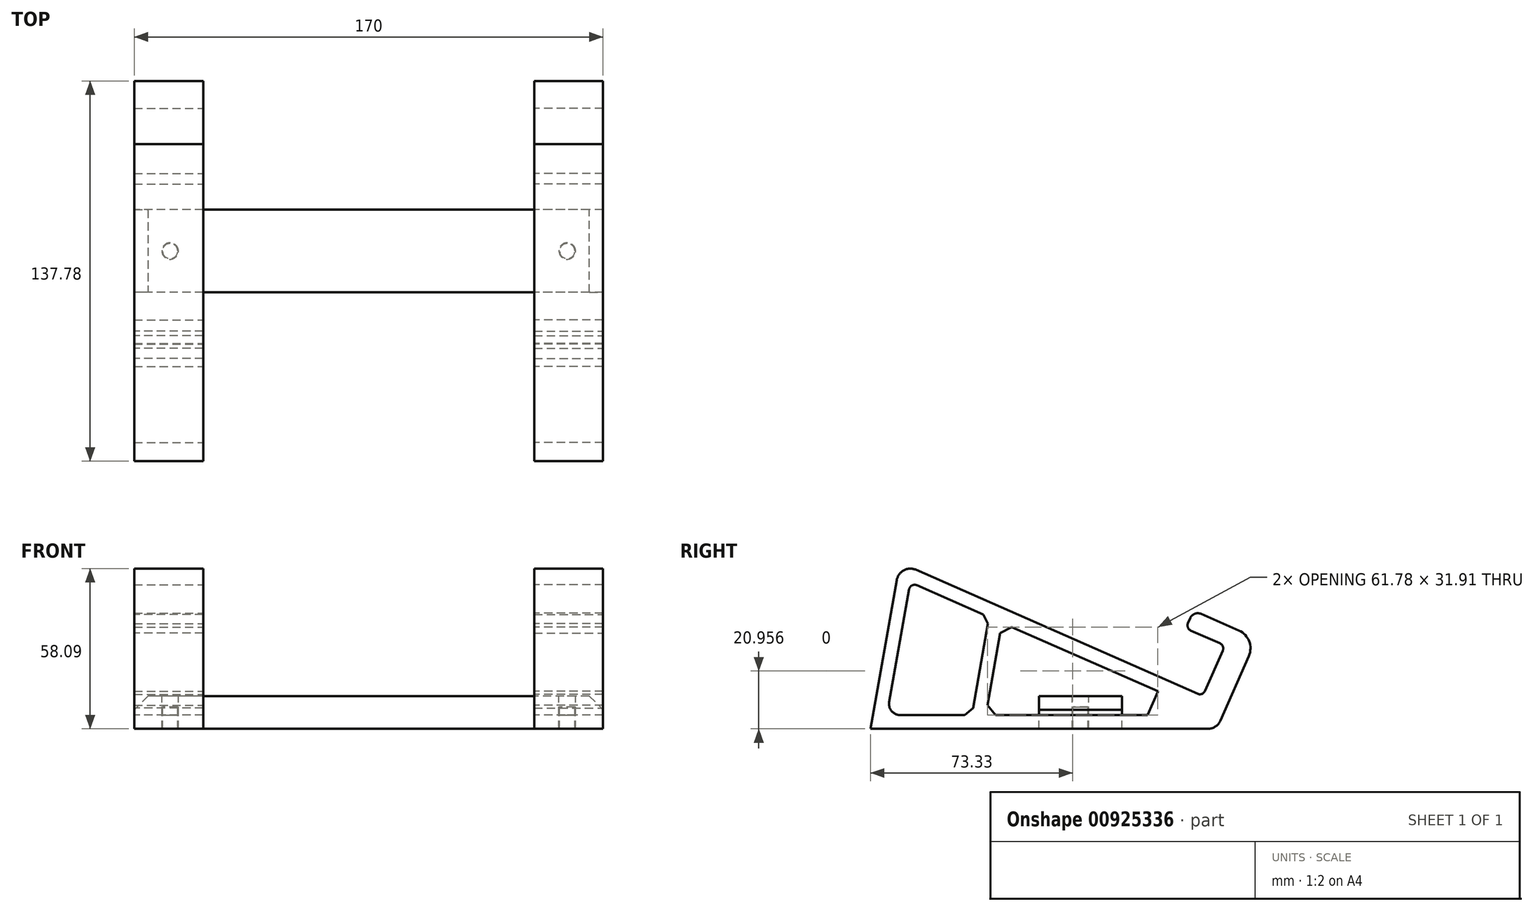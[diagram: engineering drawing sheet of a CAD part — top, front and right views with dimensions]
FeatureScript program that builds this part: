
annotation { "Feature Type Name" : "Feature", "Feature Type Description" : "" }
export const myFeature = defineFeature(function(context is Context, id is Id, definition is map)
    precondition{}
    {
        {
            var Q0;
            Q0=qCreatedBy(makeId("Right.planeOp"),FACE);
            cPlane(context, id + "F0", {"entities" : qUnion([Q0]), "cplaneType" : CPlaneType.OFFSET, "offset" : 60 * mm, "width" : 150 * mm, "height" : 150 * mm});
        }
        {
            var Q0;
            Q0=qCreatedBy(id+"F0.planeOp",FACE);
            var sketch = newSketch(context, id + "F1", { "sketchPlane" : qUnion([Q0])});
            skLineSegment(sketch, "E0", {"start": v(-1.83, 0.8) * mm, "end": v(-109.84, 48.33) * mm});
            skLineSegment(sketch, "E1", {"start": v(-109.84, 0) * mm, "end": v(0, 0) * mm, "construction": true});
            skLineSegment(sketch, "E2", {"start": v(0.8, 1.83) * mm, "end": v(7.25, 16.48) * mm});
            skLineSegment(sketch, "E3", {"start": v(6.22, 19.11) * mm, "end": v(-4.35, 23.76) * mm});
            skLineSegment(sketch, "E4", {"start": v(-5.37, 26.4) * mm, "end": v(-4.57, 28.23) * mm});
            skLineSegment(sketch, "E5", {"start": v(-0.61, 29.77) * mm, "end": v(13.12, 23.73) * mm});
            skLineSegment(sketch, "E6", {"start": v(16.7, 14.5) * mm, "end": v(0, -23.46) * mm});
            skLineSegment(sketch, "E7", {"start": v(5.09, -11.9) * mm, "end": v(-120.48, -11.9) * mm});
            skLineSegment(sketch, "E8", {"start": v(-109.84, 48.33) * mm, "end": v(-120.48, -11.9) * mm});
            skPoint(sketch, "E9.visualSharp", {"position": v(19.52, 20.9) * mm});
            skArc(sketch, "E9.filletArc", {"start": v(16.7, 14.5) * mm, "mid": v(16.82, 19.86) * mm, "end": v(13.12, 23.73) * mm});
            skPoint(sketch, "E10.visualSharp", {"position": v(-3.36, 30.98) * mm});
            skArc(sketch, "E10.filletArc", {"start": v(-0.61, 29.77) * mm, "mid": v(-2.9, 29.82) * mm, "end": v(-4.57, 28.23) * mm});
            skPoint(sketch, "E11.visualSharp", {"position": v(-6.18, 24.57) * mm});
            skArc(sketch, "E11.filletArc", {"start": v(-5.37, 26.4) * mm, "mid": v(-5.4, 24.87) * mm, "end": v(-4.35, 23.76) * mm});
            skPoint(sketch, "E12.visualSharp", {"position": v(8.05, 18.3) * mm});
            skArc(sketch, "E12.filletArc", {"start": v(7.25, 16.48) * mm, "mid": v(7.28, 18) * mm, "end": v(6.22, 19.11) * mm});
            skPoint(sketch, "E13.visualSharp", {"position": v(0, 0) * mm});
            skArc(sketch, "E13.filletArc", {"start": v(-1.83, 0.8) * mm, "mid": v(-0.3, 0.77) * mm, "end": v(0.8, 1.83) * mm});
            skSolve(sketch);
        }
        {
            var Q0;
            Q0 = qSketchRegion(id + "F1", true);
            extrude(context, id + "F2", {"entities" : qUnion([Q0]), "depth" : 25 * mm, "offsetDistance" : 25 * mm});
        }
        {
            var Q0;
            Q0=makeQuery(id+"F2.opExtrude","SWEPT_EDGE",EDGE,{"disambiguationData":[OSD([sQuery(id+"F1.wireOp",EDGE,"E0"),sQuery(id+"F1.wireOp",EDGE,"E8")])]});
            var Q1;
            Q1=makeQuery(id+"F2.opExtrude","SWEPT_EDGE",EDGE,{"disambiguationData":[OSD([sQuery(id+"F1.wireOp",EDGE,"E6"),sQuery(id+"F1.wireOp",EDGE,"E7")])]});
            fillet(context, id + "F3", {"entities" : qUnion([Q0, Q1]), "radius" : 5 * mm, "tangentPropagation" : true, "allowEdgeOverflow" : false});
        }
        {
            var Q0;
            Q0=qCreatedBy(makeId("Right.planeOp"),FACE);
            var sketch = newSketch(context, id + "F4", { "sketchPlane" : qUnion([Q0])});
            skLineSegment(sketch, "E14.0", {"start": v(-1.83, 0.8) * mm, "end": v(-104, 45.76) * mm, "construction": true});
            skLineSegment(sketch, "E15.0", {"start": v(1.83, -11.9) * mm, "end": v(-120.48, -11.9) * mm, "construction": true});
            skLineSegment(sketch, "E16.0", {"start": v(-16.26, 1.7) * mm, "end": v(-72.75, 26.55) * mm});
            skLineSegment(sketch, "E17.0", {"start": v(-20.04, -6.9) * mm, "end": v(-78.66, -6.9) * mm});
            skLineSegment(sketch, "E18", {"start": v(-16.26, 1.7) * mm, "end": v(-20.04, -6.9) * mm});
            skLineSegment(sketch, "E19.0", {"start": v(16.7, 14.5) * mm, "end": v(6.4, -8.91) * mm, "construction": true});
            skLineSegment(sketch, "E20.0", {"start": v(-106.46, 38.68) * mm, "end": v(-113.69, -2.2) * mm});
            skPoint(sketch, "E21.visualSharp", {"position": v(-106.02, 41.19) * mm});
            skArc(sketch, "E21.filletArc", {"start": v(-103.69, 40.16) * mm, "mid": v(-105.44, 40.1) * mm, "end": v(-106.46, 38.68) * mm});
            skPoint(sketch, "E22.visualSharp", {"position": v(-114.52, -6.9) * mm});
            skArc(sketch, "E22.filletArc", {"start": v(-113.69, -2.2) * mm, "mid": v(-112.81, -5.47) * mm, "end": v(-109.75, -6.9) * mm});
            skLineSegment(sketch, "E23", {"start": v(-77.46, 28.62) * mm, "end": v(-83.74, -6.9) * mm});
            skLineSegment(sketch, "E24.0", {"start": v(-72.75, 26.55) * mm, "end": v(-78.66, -6.9) * mm});
            skLineSegment(sketch, "E25.trimOffspring", {"start": v(-77.46, 28.62) * mm, "end": v(-103.69, 40.16) * mm});
            skLineSegment(sketch, "E26.trimOffspring", {"start": v(-83.74, -6.9) * mm, "end": v(-109.75, -6.9) * mm});
            skSolve(sketch);
        }
        {
            var Q0;
            Q0 = qSketchRegion(id + "F4", true);
            var Q1;
            Q1=makeQuery(id+"F2.opExtrude","CAP_FACE",FACE,{"disambiguationData":[OSD([sQuery(id+"F1.wireOp",EDGE,"E0"),sQuery(id+"F1.wireOp",EDGE,"E2"),sQuery(id+"F1.wireOp",EDGE,"E3"),sQuery(id+"F1.wireOp",EDGE,"E4"),sQuery(id+"F1.wireOp",EDGE,"E5"),sQuery(id+"F1.wireOp",EDGE,"E6"),sQuery(id+"F1.wireOp",EDGE,"E7"),sQuery(id+"F1.wireOp",EDGE,"E8"),sQuery(id+"F1.wireOp",EDGE,"E9.filletArc"),sQuery(id+"F1.wireOp",EDGE,"E10.filletArc"),sQuery(id+"F1.wireOp",EDGE,"E11.filletArc"),sQuery(id+"F1.wireOp",EDGE,"E12.filletArc"),sQuery(id+"F1.wireOp",EDGE,"E13.filletArc")])],"isStart":false});
            extrude(context, id + "F5", {"entities" : qUnion([Q0]), "operationType" : NewBodyOperationType.REMOVE, "endBound" : BoundingType.UP_TO_SURFACE, "depth" : 63 * mm, "endBoundEntityFace" : qUnion([Q1]), "offsetDistance" : 25 * mm});
        }
        {
            var Q0;
            Q0=makeQuery(id+"F5.boolean.opBoolean","COPY",EDGE,{"derivedFrom":makeQuery(id+"F5.opExtrude","SWEPT_EDGE",EDGE,{"disambiguationData":[OSD([sQuery(id+"F4.wireOp",EDGE,"E23"),sQuery(id+"F4.wireOp",EDGE,"E25.trimOffspring")])]})});
            var Q1;
            Q1=makeQuery(id+"F5.boolean.opBoolean","COPY",EDGE,{"derivedFrom":makeQuery(id+"F5.opExtrude","SWEPT_EDGE",EDGE,{"disambiguationData":[OSD([sQuery(id+"F4.wireOp",EDGE,"E16.0"),sQuery(id+"F4.wireOp",EDGE,"E24.0")])]})});
            var Q2;
            Q2=makeQuery(id+"F5.boolean.opBoolean","COPY",EDGE,{"derivedFrom":makeQuery(id+"F5.opExtrude","SWEPT_EDGE",EDGE,{"disambiguationData":[OSD([sQuery(id+"F4.wireOp",EDGE,"E23"),sQuery(id+"F4.wireOp",EDGE,"E26.trimOffspring")])]})});
            var Q3;
            Q3=makeQuery(id+"F5.boolean.opBoolean","COPY",EDGE,{"derivedFrom":makeQuery(id+"F5.opExtrude","SWEPT_EDGE",EDGE,{"disambiguationData":[OSD([sQuery(id+"F4.wireOp",EDGE,"E17.0"),sQuery(id+"F4.wireOp",EDGE,"E24.0")])]})});
            chamfer(context, id + "F6", {"entities" : qUnion([Q0, Q1, Q2, Q3]), "width" : 3 * mm, "tangentPropagation" : true});
        }
        {
            var Q0;
            Q0=makeQuery(id+"F2.opExtrude","SWEPT_BODY",BODY,{"disambiguationData":[OSD([sQuery(id+"F1.wireOp",EDGE,"E0"),sQuery(id+"F1.wireOp",EDGE,"E2"),sQuery(id+"F1.wireOp",EDGE,"E3"),sQuery(id+"F1.wireOp",EDGE,"E4"),sQuery(id+"F1.wireOp",EDGE,"E5"),sQuery(id+"F1.wireOp",EDGE,"E6"),sQuery(id+"F1.wireOp",EDGE,"E7"),sQuery(id+"F1.wireOp",EDGE,"E8"),sQuery(id+"F1.wireOp",EDGE,"E9.filletArc"),sQuery(id+"F1.wireOp",EDGE,"E10.filletArc"),sQuery(id+"F1.wireOp",EDGE,"E11.filletArc"),sQuery(id+"F1.wireOp",EDGE,"E12.filletArc"),sQuery(id+"F1.wireOp",EDGE,"E13.filletArc")])]});
            var Q1;
            Q1=qCreatedBy(makeId("Right.planeOp"),FACE);
            mirror(context, id + "F7", {"entities" : qUnion([Q0]), "mirrorPlane" : qUnion([Q1])});
        }
        {
            var Q0;
            Q0=qCreatedBy(makeId("Top.planeOp"),FACE);
            var sketch = newSketch(context, id + "F8", { "sketchPlane" : qUnion([Q0])});
            skLineSegment(sketch, "E27.bottom", {"start": v(85, -59.33) * mm, "end": v(-85, -59.33) * mm});
            skLineSegment(sketch, "E27.top", {"start": v(85, -29.33) * mm, "end": v(-85, -29.33) * mm});
            skLineSegment(sketch, "E27.left", {"start": v(85, -59.33) * mm, "end": v(85, -29.33) * mm});
            skLineSegment(sketch, "E27.right", {"start": v(-85, -59.33) * mm, "end": v(-85, -29.33) * mm});
            skPoint(sketch, "E27.middle", {"position": v(0, -44.33) * mm});
            skSolve(sketch);
        }
        {
            var Q0;
            Q0=makeQuery(id+"F8.imprint","IMPRINT",FACE,{"disambiguationData":[TD([[makeQuery(id+"F8.imprint","IMPRINT",EDGE,{"derivedFrom":sQuery(id+"F8.wireOp",EDGE,"E27.bottom")}),-1.0]])]});
            var Q1;
            Q1=makeQuery(id+"F2.opExtrude","SWEPT_FACE",FACE,{"disambiguationData":[OSD([sQuery(id+"F1.wireOp",EDGE,"E7")])]});
            extrude(context, id + "F9", {"entities" : qUnion([Q0]), "endBound" : BoundingType.UP_TO_SURFACE, "oppositeDirection" : true, "depth" : 25 * mm, "endBoundEntityFace" : qUnion([Q1]), "offsetDistance" : 25 * mm});
        }
        {
            var Q0;
            Q0=makeQuery(id+"F9.opExtrude","CAP_EDGE",EDGE,{"disambiguationData":[OSD([sQuery(id+"F8.wireOp",EDGE,"E27.left")])],"isStart":true});
            var Q1;
            Q1=makeQuery(id+"F9.opExtrude","CAP_EDGE",EDGE,{"disambiguationData":[OSD([sQuery(id+"F8.wireOp",EDGE,"E27.right")])],"isStart":true});
            chamfer(context, id + "F10", {"entities" : qUnion([Q0, Q1]), "width" : 5 * mm, "tangentPropagation" : true});
        }
        {
            var Q0;
            Q0=makeQuery(id+"F7.opPattern","COPY",BODY,{"derivedFrom":makeQuery(id+"F2.opExtrude","SWEPT_BODY",BODY,{"disambiguationData":[OSD([sQuery(id+"F1.wireOp",EDGE,"E0"),sQuery(id+"F1.wireOp",EDGE,"E2"),sQuery(id+"F1.wireOp",EDGE,"E3"),sQuery(id+"F1.wireOp",EDGE,"E4"),sQuery(id+"F1.wireOp",EDGE,"E5"),sQuery(id+"F1.wireOp",EDGE,"E6"),sQuery(id+"F1.wireOp",EDGE,"E7"),sQuery(id+"F1.wireOp",EDGE,"E8"),sQuery(id+"F1.wireOp",EDGE,"E9.filletArc"),sQuery(id+"F1.wireOp",EDGE,"E10.filletArc"),sQuery(id+"F1.wireOp",EDGE,"E11.filletArc"),sQuery(id+"F1.wireOp",EDGE,"E12.filletArc"),sQuery(id+"F1.wireOp",EDGE,"E13.filletArc")])]}),"instanceName":"1"});
            var Q1;
            Q1=makeQuery(id+"F2.opExtrude","SWEPT_BODY",BODY,{"disambiguationData":[OSD([sQuery(id+"F1.wireOp",EDGE,"E0"),sQuery(id+"F1.wireOp",EDGE,"E2"),sQuery(id+"F1.wireOp",EDGE,"E3"),sQuery(id+"F1.wireOp",EDGE,"E4"),sQuery(id+"F1.wireOp",EDGE,"E5"),sQuery(id+"F1.wireOp",EDGE,"E6"),sQuery(id+"F1.wireOp",EDGE,"E7"),sQuery(id+"F1.wireOp",EDGE,"E8"),sQuery(id+"F1.wireOp",EDGE,"E9.filletArc"),sQuery(id+"F1.wireOp",EDGE,"E10.filletArc"),sQuery(id+"F1.wireOp",EDGE,"E11.filletArc"),sQuery(id+"F1.wireOp",EDGE,"E12.filletArc"),sQuery(id+"F1.wireOp",EDGE,"E13.filletArc")])]});
            var Q2;
            Q2=makeQuery(id+"F9.opExtrude","SWEPT_BODY",BODY,{"disambiguationData":[OSD([sQuery(id+"F8.wireOp",EDGE,"E27.bottom"),sQuery(id+"F8.wireOp",EDGE,"E27.top"),sQuery(id+"F8.wireOp",EDGE,"E27.left"),sQuery(id+"F8.wireOp",EDGE,"E27.right")])]});
            booleanBodies(context, id + "F11", {"operationType" : BooleanOperationType.SUBTRACTION, "tools" : qUnion([Q0, Q1]), "targets" : qUnion([Q2]), "keepTools" : true});
        }
        {
            var Q0;
            Q0=qCreatedBy(makeId("Top.planeOp"),FACE);
            var sketch = newSketch(context, id + "F12", { "sketchPlane" : qUnion([Q0])});
            skCircle(sketch, "E28", {"center": v(-72, -44.33) * mm, "radius": 3 * mm});
            skCircle(sketch, "E29.MirrorC", {"center": v(72, -44.33) * mm, "radius": 3 * mm});
            skSolve(sketch);
        }
        {
            var Q0;
            Q0 = qSketchRegion(id + "F12", true);
            extrude(context, id + "F13", {"entities" : qUnion([Q0]), "operationType" : NewBodyOperationType.REMOVE, "oppositeDirection" : true, "depth" : 25 * mm, "offsetDistance" : 25 * mm});
        }
        {
            var Q0;
            Q0=qCreatedBy(makeId("Top.planeOp"),FACE);
            var sketch = newSketch(context, id + "F14", { "sketchPlane" : qUnion([Q0])});
            skCircle(sketch, "E30.0", {"center": v(-72, -44.33) * mm, "radius": 6 * mm, "construction": true});
            skCircle(sketch, "E31.0", {"center": v(72, -44.33) * mm, "radius": 6 * mm, "construction": true});
            skLineSegment(sketch, "E32.0", {"start": v(85, -24.33) * mm, "end": v(-85, -24.33) * mm, "construction": true});
            skLineSegment(sketch, "E32.1", {"start": v(85, -64.33) * mm, "end": v(85, -24.33) * mm, "construction": true});
            skLineSegment(sketch, "E32.2", {"start": v(-85, -64.33) * mm, "end": v(85, -64.33) * mm, "construction": true});
            skLineSegment(sketch, "E32.3", {"start": v(-85, -24.33) * mm, "end": v(-85, -64.33) * mm, "construction": true});
            skCircle(sketch, "E33", {"center": v(-72, -44.33) * mm, "radius": 2.75 * mm});
            skCircle(sketch, "E34", {"center": v(72, -44.33) * mm, "radius": 2.75 * mm});
            skSolve(sketch);
        }
        {
            var Q0;
            Q0 = qSketchRegion(id + "F14", true);
            var Q1;
            Q1=makeQuery(id+"F2.opExtrude","SWEPT_FACE",FACE,{"disambiguationData":[OSD([sQuery(id+"F1.wireOp",EDGE,"E7")])]});
            extrude(context, id + "F15", {"entities" : qUnion([Q0]), "operationType" : NewBodyOperationType.ADD, "endBound" : BoundingType.UP_TO_SURFACE, "oppositeDirection" : true, "depth" : 25 * mm, "endBoundEntityFace" : qUnion([Q1]), "offsetDistance" : 25 * mm, "hasSecondDirection" : true, "secondDirectionOppositeDirection" : true, "secondDirectionDepth" : 4 * mm});
        }
    });
